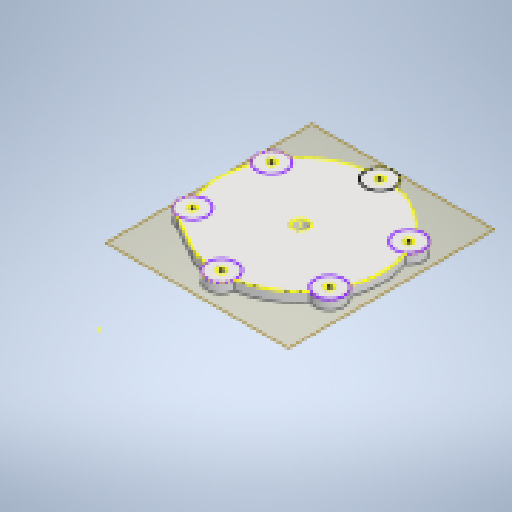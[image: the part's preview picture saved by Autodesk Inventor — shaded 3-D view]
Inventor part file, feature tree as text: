
AUTODESK INVENTOR PART (.ipt)
format: ipt  version: 2023.1 (Build 271208000, 208)  size: 357,376 bytes
history: native  units: mm
features: extrude x7, other x5, sketch x4, pattern_circular x4, chamfer x3, plane x2
ambient origin geometry x8: Origin, YZ Plane, XZ Plane, XY Plane, X Axis, Y Axis, Z Axis, Center Point
bodies: Body1 (feature_tree)
feature tree (25):
  plane  "Work Plane1"
  sketch  "Sketch3"  dims[d3=38.0mm d4=2.2mm]
  extrude  "Extrusion2"  Depth=2.2mm
  extrude  "Extrusion3"  Depth=3.0mm TaperAngle=0.0deg
  pattern_circular  "Circular Pattern1"  Count=6 Angle=360.0deg
  extrude  "Extrusion4"  Depth=60.0mm TaperAngle=360.0deg
  pattern_circular  "Circular Pattern2"  [2 undecoded]
  extrude  "Extrusion5"  Depth=13.0mm TaperAngle=0.0deg
  extrude  "Extrusion6"  Depth=1.5mm
  plane  "Work Plane2"
  extrude  "Extrusion8"  Depth=13.0mm TaperAngle=0.0deg
  pattern_circular  "Circular Pattern3"  [2 undecoded]
  extrude  "Extrusion9"  Depth=2.0mm
  pattern_circular  "Circular Pattern4"  [2 undecoded]
  chamfer  "Chamfer1"  Distance=60.0mm Angle=360.0deg
  chamfer  "Chamfer2"  Distance=4.75mm
  chamfer  "Chamfer3"  Distance=60.0mm Angle=360.0deg
  sketch  "Sketch4"  dims[d5=4.5mm d6=3.0mm d7=0.0mm]
  other  "Work Axis1"
  other  "Work Axis2"
  sketch  "Sketch5"  dims[d8=5.0mm d9=0.0mm d10=60.0mm d11=360.0deg]
  sketch  "Sketch6"  dims[d13=5.0mm d14=0.0mm d15=60.0mm d16=360.0deg d18=13.0mm d19=13.0mm d20=0.0mm d21=1.5mm d22=13.0mm d23=0.0mm d26=2.0mm d27=2.0mm d28=2.0mm d29=0.0mm d30=60.0mm d31=360.0deg d33=4.75mm d34=0.0mm d35=60.0mm d36=360.0deg d38=1.5mm d39=2.0mm d40=45.0deg d41=4.0mm d42=2.0mm d43=45.0deg d44=4.0mm d45=2.0mm d46=45.0deg d47=0.5mm d48=0.872665mm d49=0.5mm d50=0.872665mm]
  other  "<userpath>\Documents\WaterPump\Assembly1.iam"
  other  "Assembly1.iam"
  other  "case:1"
note: 6 required parameter values undecoded (feature->parameter linkage not recoverable at this tier; creation-order binding heuristic only, values carry confidence <= 0.55)
